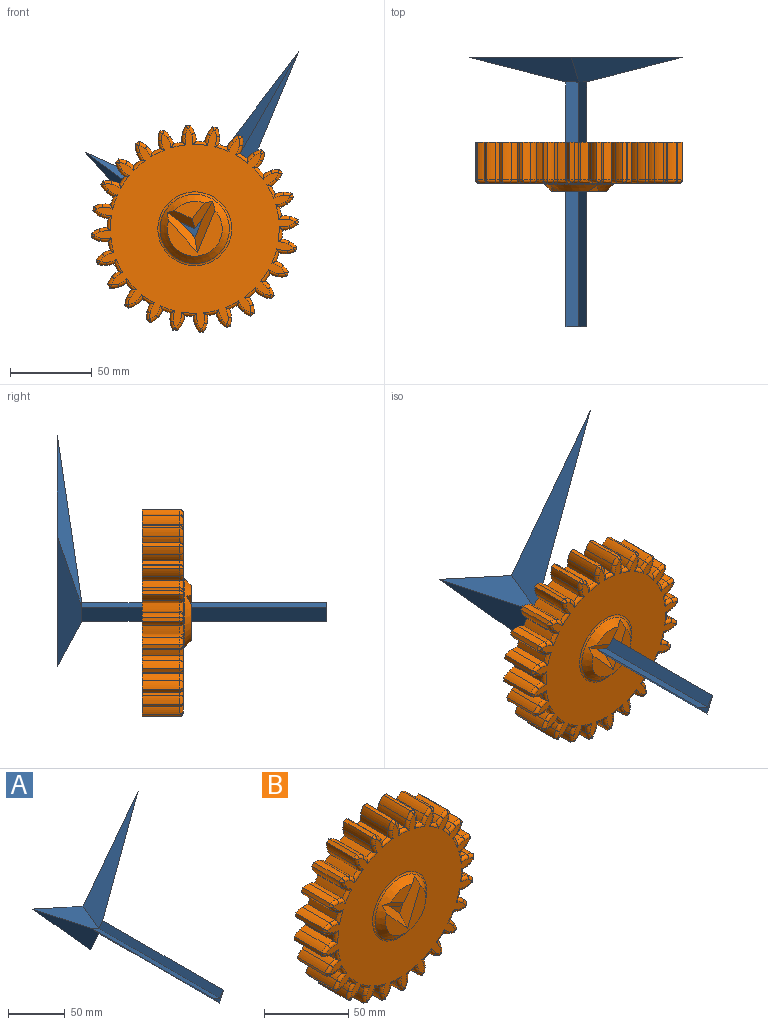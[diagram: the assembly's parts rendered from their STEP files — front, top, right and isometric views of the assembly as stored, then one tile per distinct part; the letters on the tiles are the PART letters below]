
ASSEMBLY  parts=2 mates=1
PART A: 10 faces, bbox 130.9x165x141.5 mm
  f0: plane 150x6.29mm, normal (-0.8,0,0.61), area 1184.6mm2, adj f1,f3,f4,f5
  f1: plane 150x7.89mm, normal (0.41,0,0.91), area 1299.2mm2, adj f0,f2,f4,f8
  f2: plane 150x8.75mm, normal (-0.74,0,-0.67), area 1767mm2, adj f1,f3,f4,f7
  f3: plane 150x11.46mm, normal (0.92,0,-0.38), area 1861.9mm2, adj f0,f2,f4,f6
  f4: plane 12.66x11.46mm, normal (0,-1,0), area 32.7mm2, adj f0,f1,f2,f3
  f5: plane 108.65x68.42mm, normal (-0.56,-0.71,0.43), area 1283.2mm2, adj f0,f6,f8,f9
  f6: plane 141.47x63.72mm, normal (0.65,-0.71,-0.27), area 1757.4mm2, adj f3,f5,f7,f9
  f7: plane 79.84x71.93mm, normal (-0.53,-0.71,-0.47), area 1264.8mm2, adj f2,f6,f8,f9
  f8: plane 67.21x47.02mm, normal (0.29,-0.71,0.64), area 820.2mm2, adj f1,f5,f7,f9
  f9: plane 141.47x130.94mm, normal (0,1,0), area 3657mm2, adj f5,f6,f7,f8
PART B: 302 faces, bbox 127.2x30x127.2 mm
  f0: plane 18.26x10.6mm, normal (0,-1,0), area 107.7mm2, adj f154,f155,f156
  f1: cylinder r=53.72mm len=23mm, axis (0,1,0), area 121.2mm2, adj f29,f31,f96,f289
  f2: cylinder r=53.72mm len=23mm, axis (0,1,0), area 121.2mm2, adj f31,f91,f95,f277
  f3: cylinder r=53.72mm len=23mm, axis (0,1,0), area 121.2mm2, adj f31,f86,f90,f265
  f4: cylinder r=53.72mm len=23mm, axis (0,1,0), area 121.2mm2, adj f31,f81,f85,f253
  f5: cylinder r=53.72mm len=23mm, axis (0,1,0), area 121.2mm2, adj f31,f76,f80,f241
  f6: cylinder r=53.72mm len=23mm, axis (0,1,0), area 121.2mm2, adj f31,f71,f75,f229
  f7: cylinder r=53.72mm len=23mm, axis (0,1,0), area 121.2mm2, adj f31,f66,f70,f217
  f8: cylinder r=53.72mm len=23mm, axis (0,1,0), area 121.2mm2, adj f31,f61,f65,f205
  f9: cylinder r=53.72mm len=23mm, axis (0,1,0), area 121.2mm2, adj f31,f56,f60,f193
  f10: cylinder r=53.72mm len=23mm, axis (0,1,0), area 121.2mm2, adj f31,f51,f55,f181
  f11: cylinder r=53.72mm len=23mm, axis (0,1,0), area 121.2mm2, adj f31,f46,f50,f169
  f12: cylinder r=53.72mm len=23mm, axis (0,1,0), area 121.2mm2, adj f31,f41,f45,f157
  f13: cylinder r=53.72mm len=23mm, axis (0,1,0), area 121.2mm2, adj f31,f40,f147,f168
  f14: cylinder r=53.72mm len=23mm, axis (0,1,0), area 121.2mm2, adj f31,f146,f151,f180
  f15: cylinder r=53.72mm len=23mm, axis (0,1,0), area 121.2mm2, adj f31,f141,f145,f192
  f16: cylinder r=53.72mm len=23mm, axis (0,1,0), area 121.2mm2, adj f31,f136,f140,f204
  f17: cylinder r=53.72mm len=23mm, axis (0,1,0), area 121.2mm2, adj f31,f131,f135,f216
  f18: cylinder r=53.72mm len=23mm, axis (0,1,0), area 121.2mm2, adj f31,f126,f130,f228
  f19: cylinder r=53.72mm len=23mm, axis (0,1,0), area 121.2mm2, adj f31,f121,f125,f240
  f20: cylinder r=53.72mm len=23mm, axis (0,1,0), area 121.2mm2, adj f31,f116,f120,f252
  f21: cylinder r=53.72mm len=23mm, axis (0,1,0), area 121.2mm2, adj f31,f111,f115,f264
  f22: cylinder r=53.72mm len=23mm, axis (0,1,0), area 121.2mm2, adj f31,f106,f110,f276
  f23: cylinder r=53.72mm len=23mm, axis (0,1,0), area 121.2mm2, adj f31,f100,f105,f288
  f24: cylinder r=53.72mm len=23mm, axis (0,1,0), area 121.2mm2, adj f25,f31,f101,f300
  f25: cylinder r=14.37mm len=23mm, axis (0,1,0), area 116.5mm2, adj f24,f26,f31,f299
  f26: cylinder r=14.83mm len=23mm, axis (0,1,0), area 128.5mm2, adj f25,f27,f31,f297
  f27: cylinder r=36.75mm len=23mm, axis (0,1,0), area 59.7mm2, adj f26,f28,f31,f295
  f28: cylinder r=14.83mm len=23mm, axis (0,1,0), area 128.5mm2, adj f27,f29,f31,f293
  f29: cylinder r=14.37mm len=23mm, axis (0,1,0), area 116.5mm2, adj f1,f28,f31,f291
  f30: plane 122.71x122.71mm, normal (0,-1,0), area 7685.4mm2, adj f157,f158,f159,f160,f161,f162,f163,f164
  f31: plane 126.87x126.87mm, normal (0,1,0), area 10687.8mm2, adj f1,f2,f3,f4,f5,f6,f7,f8
  f32: plane 25x6.29mm, normal (0.8,0,-0.61), area 197.4mm2, adj f31,f33,f36,f155
  f33: plane 25x11.46mm, normal (-0.92,0,0.38), area 310.3mm2, adj f31,f32,f34,f152
  f34: plane 25x8.75mm, normal (0.74,0,0.67), area 294.5mm2, adj f31,f33,f36,f153
  f35: plane 33.61x28.22mm, normal (0,-1,0), area 384mm2, adj f152,f153,f154
  f36: plane 25x7.89mm, normal (-0.41,0,-0.91), area 216.5mm2, adj f31,f32,f34,f156
  f37: cylinder r=14.83mm len=23mm, axis (0,1,0), area 128.5mm2, adj f31,f38,f41,f160
  f38: cylinder r=36.75mm len=23mm, axis (0,1,0), area 59.7mm2, adj f31,f37,f39,f162
  f39: cylinder r=14.83mm len=23mm, axis (0,1,0), area 128.5mm2, adj f31,f38,f40,f164
  f40: cylinder r=14.37mm len=23mm, axis (0,1,0), area 116.5mm2, adj f13,f31,f39,f166
  f41: cylinder r=14.37mm len=23mm, axis (0,1,0), area 116.5mm2, adj f12,f31,f37,f158
  f42: cylinder r=14.83mm len=23mm, axis (0,1,0), area 128.5mm2, adj f31,f43,f46,f165
  f43: cylinder r=36.75mm len=23mm, axis (0,1,0), area 59.7mm2, adj f31,f42,f44,f163
  f44: cylinder r=14.83mm len=23mm, axis (0,1,0), area 128.5mm2, adj f31,f43,f45,f161
  f45: cylinder r=14.37mm len=23mm, axis (0,1,0), area 116.5mm2, adj f12,f31,f44,f159
  f46: cylinder r=14.37mm len=23mm, axis (0,1,0), area 116.5mm2, adj f11,f31,f42,f167
  f47: cylinder r=14.83mm len=23mm, axis (0,1,0), area 128.5mm2, adj f31,f48,f51,f177
  f48: cylinder r=36.75mm len=23mm, axis (0,1,0), area 59.7mm2, adj f31,f47,f49,f175
  f49: cylinder r=14.83mm len=23mm, axis (0,1,0), area 128.5mm2, adj f31,f48,f50,f173
  f50: cylinder r=14.37mm len=23mm, axis (0,1,0), area 116.5mm2, adj f11,f31,f49,f171
  f51: cylinder r=14.37mm len=23mm, axis (0,1,0), area 116.5mm2, adj f10,f31,f47,f179
  f52: cylinder r=14.83mm len=23mm, axis (0,1,0), area 128.5mm2, adj f31,f53,f56,f189
  f53: cylinder r=36.75mm len=23mm, axis (0,1,0), area 59.7mm2, adj f31,f52,f54,f187
  f54: cylinder r=14.83mm len=23mm, axis (0,1,0), area 128.5mm2, adj f31,f53,f55,f185
  f55: cylinder r=14.37mm len=23mm, axis (0,1,0), area 116.5mm2, adj f10,f31,f54,f183
  f56: cylinder r=14.37mm len=23mm, axis (0,1,0), area 116.5mm2, adj f9,f31,f52,f191
  f57: cylinder r=14.83mm len=23mm, axis (0,1,0), area 128.5mm2, adj f31,f58,f61,f201
  f58: cylinder r=36.75mm len=23mm, axis (0,1,0), area 59.7mm2, adj f31,f57,f59,f199
  f59: cylinder r=14.83mm len=23mm, axis (0,1,0), area 128.5mm2, adj f31,f58,f60,f197
  f60: cylinder r=14.37mm len=23mm, axis (0,1,0), area 116.5mm2, adj f9,f31,f59,f195
  f61: cylinder r=14.37mm len=23mm, axis (0,1,0), area 116.5mm2, adj f8,f31,f57,f203
  f62: cylinder r=14.83mm len=23mm, axis (0,1,0), area 128.5mm2, adj f31,f63,f66,f213
  f63: cylinder r=36.75mm len=23mm, axis (0,1,0), area 59.7mm2, adj f31,f62,f64,f211
  f64: cylinder r=14.83mm len=23mm, axis (0,1,0), area 128.5mm2, adj f31,f63,f65,f209
  f65: cylinder r=14.37mm len=23mm, axis (0,1,0), area 116.5mm2, adj f8,f31,f64,f207
  f66: cylinder r=14.37mm len=23mm, axis (0,1,0), area 116.5mm2, adj f7,f31,f62,f215
  f67: cylinder r=14.83mm len=23mm, axis (0,1,0), area 128.5mm2, adj f31,f68,f71,f225
  f68: cylinder r=36.75mm len=23mm, axis (0,1,0), area 59.7mm2, adj f31,f67,f69,f223
  f69: cylinder r=14.83mm len=23mm, axis (0,1,0), area 128.5mm2, adj f31,f68,f70,f221
  f70: cylinder r=14.37mm len=23mm, axis (0,1,0), area 116.5mm2, adj f7,f31,f69,f219
  f71: cylinder r=14.37mm len=23mm, axis (0,1,0), area 116.5mm2, adj f6,f31,f67,f227
  f72: cylinder r=14.83mm len=23mm, axis (0,1,0), area 128.5mm2, adj f31,f73,f76,f237
  f73: cylinder r=36.75mm len=23mm, axis (0,1,0), area 59.7mm2, adj f31,f72,f74,f235
  f74: cylinder r=14.83mm len=23mm, axis (0,1,0), area 128.5mm2, adj f31,f73,f75,f233
  f75: cylinder r=14.37mm len=23mm, axis (0,1,0), area 116.5mm2, adj f6,f31,f74,f231
  f76: cylinder r=14.37mm len=23mm, axis (0,1,0), area 116.5mm2, adj f5,f31,f72,f239
  f77: cylinder r=14.83mm len=23mm, axis (0,1,0), area 128.5mm2, adj f31,f78,f81,f249
  f78: cylinder r=36.75mm len=23mm, axis (0,1,0), area 59.7mm2, adj f31,f77,f79,f247
  f79: cylinder r=14.83mm len=23mm, axis (0,1,0), area 128.5mm2, adj f31,f78,f80,f245
  f80: cylinder r=14.37mm len=23mm, axis (0,1,0), area 116.5mm2, adj f5,f31,f79,f243
  f81: cylinder r=14.37mm len=23mm, axis (0,1,0), area 116.5mm2, adj f4,f31,f77,f251
  f82: cylinder r=14.83mm len=23mm, axis (0,1,0), area 128.5mm2, adj f31,f83,f86,f261
  f83: cylinder r=36.75mm len=23mm, axis (0,1,0), area 59.7mm2, adj f31,f82,f84,f259
  f84: cylinder r=14.83mm len=23mm, axis (0,1,0), area 128.5mm2, adj f31,f83,f85,f257
  f85: cylinder r=14.37mm len=23mm, axis (0,1,0), area 116.5mm2, adj f4,f31,f84,f255
  f86: cylinder r=14.37mm len=23mm, axis (0,1,0), area 116.5mm2, adj f3,f31,f82,f263
  f87: cylinder r=14.83mm len=23mm, axis (0,1,0), area 128.5mm2, adj f31,f88,f91,f273
  f88: cylinder r=36.75mm len=23mm, axis (0,1,0), area 59.7mm2, adj f31,f87,f89,f271
  f89: cylinder r=14.83mm len=23mm, axis (0,1,0), area 128.5mm2, adj f31,f88,f90,f269
  f90: cylinder r=14.37mm len=23mm, axis (0,1,0), area 116.5mm2, adj f3,f31,f89,f267
  f91: cylinder r=14.37mm len=23mm, axis (0,1,0), area 116.5mm2, adj f2,f31,f87,f275
  f92: cylinder r=14.83mm len=23mm, axis (0,1,0), area 128.5mm2, adj f31,f93,f96,f285
  f93: cylinder r=36.75mm len=23mm, axis (0,1,0), area 59.7mm2, adj f31,f92,f94,f283
  f94: cylinder r=14.83mm len=23mm, axis (0,1,0), area 128.5mm2, adj f31,f93,f95,f281
  f95: cylinder r=14.37mm len=23mm, axis (0,1,0), area 116.5mm2, adj f2,f31,f94,f279
  f96: cylinder r=14.37mm len=23mm, axis (0,1,0), area 116.5mm2, adj f1,f31,f92,f287
  f97: cylinder r=14.83mm len=23mm, axis (0,1,0), area 128.5mm2, adj f31,f98,f100,f292
  f98: cylinder r=36.75mm len=23mm, axis (0,1,0), area 59.7mm2, adj f31,f97,f99,f294
  f99: cylinder r=14.83mm len=23mm, axis (0,1,0), area 128.5mm2, adj f31,f98,f101,f296
  f100: cylinder r=14.37mm len=23mm, axis (0,1,0), area 116.5mm2, adj f23,f31,f97,f290
  f101: cylinder r=14.37mm len=23mm, axis (0,1,0), area 116.5mm2, adj f24,f31,f99,f298
  f102: cylinder r=14.83mm len=23mm, axis (0,1,0), area 128.5mm2, adj f31,f103,f106,f280
  f103: cylinder r=36.75mm len=23mm, axis (0,1,0), area 59.7mm2, adj f31,f102,f104,f282
  f104: cylinder r=14.83mm len=23mm, axis (0,1,0), area 128.5mm2, adj f31,f103,f105,f284
  f105: cylinder r=14.37mm len=23mm, axis (0,1,0), area 116.5mm2, adj f23,f31,f104,f286
  f106: cylinder r=14.37mm len=23mm, axis (0,1,0), area 116.5mm2, adj f22,f31,f102,f278
  f107: cylinder r=14.83mm len=23mm, axis (0,1,0), area 128.5mm2, adj f31,f108,f111,f268
  f108: cylinder r=36.75mm len=23mm, axis (0,1,0), area 59.7mm2, adj f31,f107,f109,f270
  f109: cylinder r=14.83mm len=23mm, axis (0,1,0), area 128.5mm2, adj f31,f108,f110,f272
  f110: cylinder r=14.37mm len=23mm, axis (0,1,0), area 116.5mm2, adj f22,f31,f109,f274
  f111: cylinder r=14.37mm len=23mm, axis (0,1,0), area 116.5mm2, adj f21,f31,f107,f266
  f112: cylinder r=14.83mm len=23mm, axis (0,1,0), area 128.5mm2, adj f31,f113,f116,f256
  f113: cylinder r=36.75mm len=23mm, axis (0,1,0), area 59.7mm2, adj f31,f112,f114,f258
  f114: cylinder r=14.83mm len=23mm, axis (0,1,0), area 128.5mm2, adj f31,f113,f115,f260
  f115: cylinder r=14.37mm len=23mm, axis (0,1,0), area 116.5mm2, adj f21,f31,f114,f262
  f116: cylinder r=14.37mm len=23mm, axis (0,1,0), area 116.5mm2, adj f20,f31,f112,f254
  f117: cylinder r=14.83mm len=23mm, axis (0,1,0), area 128.5mm2, adj f31,f118,f121,f244
  f118: cylinder r=36.75mm len=23mm, axis (0,1,0), area 59.7mm2, adj f31,f117,f119,f246
  f119: cylinder r=14.83mm len=23mm, axis (0,1,0), area 128.5mm2, adj f31,f118,f120,f248
  f120: cylinder r=14.37mm len=23mm, axis (0,1,0), area 116.5mm2, adj f20,f31,f119,f250
  f121: cylinder r=14.37mm len=23mm, axis (0,1,0), area 116.5mm2, adj f19,f31,f117,f242
  f122: cylinder r=14.83mm len=23mm, axis (0,1,0), area 128.5mm2, adj f31,f123,f126,f232
  f123: cylinder r=36.75mm len=23mm, axis (0,1,0), area 59.7mm2, adj f31,f122,f124,f234
  f124: cylinder r=14.83mm len=23mm, axis (0,1,0), area 128.5mm2, adj f31,f123,f125,f236
  f125: cylinder r=14.37mm len=23mm, axis (0,1,0), area 116.5mm2, adj f19,f31,f124,f238
  f126: cylinder r=14.37mm len=23mm, axis (0,1,0), area 116.5mm2, adj f18,f31,f122,f230
  f127: cylinder r=14.83mm len=23mm, axis (0,1,0), area 128.5mm2, adj f31,f128,f131,f220
  f128: cylinder r=36.75mm len=23mm, axis (0,1,0), area 59.7mm2, adj f31,f127,f129,f222
  f129: cylinder r=14.83mm len=23mm, axis (0,1,0), area 128.5mm2, adj f31,f128,f130,f224
  f130: cylinder r=14.37mm len=23mm, axis (0,1,0), area 116.5mm2, adj f18,f31,f129,f226
  f131: cylinder r=14.37mm len=23mm, axis (0,1,0), area 116.5mm2, adj f17,f31,f127,f218
  f132: cylinder r=14.83mm len=23mm, axis (0,1,0), area 128.5mm2, adj f31,f133,f136,f208
  f133: cylinder r=36.75mm len=23mm, axis (0,1,0), area 59.7mm2, adj f31,f132,f134,f210
  f134: cylinder r=14.83mm len=23mm, axis (0,1,0), area 128.5mm2, adj f31,f133,f135,f212
  f135: cylinder r=14.37mm len=23mm, axis (0,1,0), area 116.5mm2, adj f17,f31,f134,f214
  f136: cylinder r=14.37mm len=23mm, axis (0,1,0), area 116.5mm2, adj f16,f31,f132,f206
  f137: cylinder r=14.83mm len=23mm, axis (0,1,0), area 128.5mm2, adj f31,f138,f141,f196
  f138: cylinder r=36.75mm len=23mm, axis (0,1,0), area 59.7mm2, adj f31,f137,f139,f198
  f139: cylinder r=14.83mm len=23mm, axis (0,1,0), area 128.5mm2, adj f31,f138,f140,f200
  f140: cylinder r=14.37mm len=23mm, axis (0,1,0), area 116.5mm2, adj f16,f31,f139,f202
  f141: cylinder r=14.37mm len=23mm, axis (0,1,0), area 116.5mm2, adj f15,f31,f137,f194
  f142: cylinder r=14.83mm len=23mm, axis (0,1,0), area 128.5mm2, adj f31,f143,f146,f184
  f143: cylinder r=36.75mm len=23mm, axis (0,1,0), area 59.7mm2, adj f31,f142,f144,f186
  f144: cylinder r=14.83mm len=23mm, axis (0,1,0), area 128.5mm2, adj f31,f143,f145,f188
  f145: cylinder r=14.37mm len=23mm, axis (0,1,0), area 116.5mm2, adj f15,f31,f144,f190
  f146: cylinder r=14.37mm len=23mm, axis (0,1,0), area 116.5mm2, adj f14,f31,f142,f182
  f147: cylinder r=14.37mm len=23mm, axis (0,1,0), area 116.5mm2, adj f13,f31,f148,f170
  f148: cylinder r=14.83mm len=23mm, axis (0,1,0), area 128.5mm2, adj f31,f147,f149,f172
  f149: cylinder r=36.75mm len=23mm, axis (0,1,0), area 59.7mm2, adj f31,f148,f150,f174
  f150: cylinder r=14.83mm len=23mm, axis (0,1,0), area 128.5mm2, adj f31,f149,f151,f176
  f151: cylinder r=14.37mm len=23mm, axis (0,1,0), area 116.5mm2, adj f14,f31,f150,f178
  f152: plane 31.4x12.33mm, normal (-0.65,-0.71,0.27), area 178.1mm2, adj f33,f35,f153,f154,f155
  f153: plane 24.47x18.34mm, normal (0.53,-0.71,0.47), area 162.5mm2, adj f34,f35,f152,f154,f156
  f154: cone r=16.8mm half-angle=45deg, axis (0,1,0), area 713mm2, adj f0,f35,f152,f153,f155,f156,f301
  f155: plane 17.01x12.52mm, normal (0.56,-0.71,-0.43), area 105.3mm2, adj f0,f32,f152,f154,f156
  f156: plane 16.76x11.19mm, normal (-0.29,-0.71,-0.64), area 99.8mm2, adj f0,f36,f153,f154,f155
  f157: torus R=51.72mm, axis (0,-1,0), area 21mm2, adj f12,f30,f158,f159
  f158: torus R=12.37mm, axis (0,-1,0), area 17.4mm2, adj f30,f41,f157,f160
  f159: torus R=12.37mm, axis (0,-1,0), area 17.4mm2, adj f30,f45,f157,f161
  f160: torus R=12.83mm, axis (0,-1,0), area 15.6mm2, adj f30,f37,f158,f162
  f161: torus R=12.83mm, axis (0,-1,0), area 15.6mm2, adj f30,f44,f159,f163
  f162: torus R=38.75mm, axis (0,-1,0), area 5.9mm2, adj f30,f38,f160,f164
  f163: torus R=38.75mm, axis (0,-1,0), area 5.9mm2, adj f30,f43,f161,f165
  f164: torus R=12.83mm, axis (0,-1,0), area 15.6mm2, adj f30,f39,f162,f166
  f165: torus R=12.83mm, axis (0,-1,0), area 15.6mm2, adj f30,f42,f163,f167
  f166: torus R=12.37mm, axis (0,-1,0), area 17.4mm2, adj f30,f40,f164,f168
  f167: torus R=12.37mm, axis (0,-1,0), area 17.4mm2, adj f30,f46,f165,f169
  f168: torus R=51.72mm, axis (0,-1,0), area 21mm2, adj f13,f30,f166,f170
  f169: torus R=51.72mm, axis (0,-1,0), area 21mm2, adj f11,f30,f167,f171
  f170: torus R=12.37mm, axis (0,-1,0), area 17.4mm2, adj f30,f147,f168,f172
  f171: torus R=12.37mm, axis (0,-1,0), area 17.4mm2, adj f30,f50,f169,f173
  f172: torus R=12.83mm, axis (0,-1,0), area 15.6mm2, adj f30,f148,f170,f174
  f173: torus R=12.83mm, axis (0,-1,0), area 15.6mm2, adj f30,f49,f171,f175
  f174: torus R=38.75mm, axis (0,-1,0), area 5.9mm2, adj f30,f149,f172,f176
  f175: torus R=38.75mm, axis (0,-1,0), area 5.9mm2, adj f30,f48,f173,f177
  f176: torus R=12.83mm, axis (0,-1,0), area 15.6mm2, adj f30,f150,f174,f178
  f177: torus R=12.83mm, axis (0,-1,0), area 15.6mm2, adj f30,f47,f175,f179
  f178: torus R=12.37mm, axis (0,-1,0), area 17.4mm2, adj f30,f151,f176,f180
  f179: torus R=12.37mm, axis (0,-1,0), area 17.4mm2, adj f30,f51,f177,f181
  f180: torus R=51.72mm, axis (0,-1,0), area 21mm2, adj f14,f30,f178,f182
  f181: torus R=51.72mm, axis (0,-1,0), area 21mm2, adj f10,f30,f179,f183
  f182: torus R=12.37mm, axis (0,-1,0), area 17.4mm2, adj f30,f146,f180,f184
  f183: torus R=12.37mm, axis (0,-1,0), area 17.4mm2, adj f30,f55,f181,f185
  f184: torus R=12.83mm, axis (0,-1,0), area 15.6mm2, adj f30,f142,f182,f186
  f185: torus R=12.83mm, axis (0,-1,0), area 15.6mm2, adj f30,f54,f183,f187
  f186: torus R=38.75mm, axis (0,-1,0), area 5.9mm2, adj f30,f143,f184,f188
  f187: torus R=38.75mm, axis (0,-1,0), area 5.9mm2, adj f30,f53,f185,f189
  f188: torus R=12.83mm, axis (0,-1,0), area 15.6mm2, adj f30,f144,f186,f190
  f189: torus R=12.83mm, axis (0,-1,0), area 15.6mm2, adj f30,f52,f187,f191
  f190: torus R=12.37mm, axis (0,-1,0), area 17.4mm2, adj f30,f145,f188,f192
  f191: torus R=12.37mm, axis (0,-1,0), area 17.4mm2, adj f30,f56,f189,f193
  f192: torus R=51.72mm, axis (0,-1,0), area 21mm2, adj f15,f30,f190,f194
  f193: torus R=51.72mm, axis (0,-1,0), area 21mm2, adj f9,f30,f191,f195
  f194: torus R=12.37mm, axis (0,-1,0), area 17.4mm2, adj f30,f141,f192,f196
  f195: torus R=12.37mm, axis (0,-1,0), area 17.4mm2, adj f30,f60,f193,f197
  f196: torus R=12.83mm, axis (0,-1,0), area 15.6mm2, adj f30,f137,f194,f198
  f197: torus R=12.83mm, axis (0,-1,0), area 15.6mm2, adj f30,f59,f195,f199
  f198: torus R=38.75mm, axis (0,-1,0), area 5.9mm2, adj f30,f138,f196,f200
  f199: torus R=38.75mm, axis (0,-1,0), area 5.9mm2, adj f30,f58,f197,f201
  f200: torus R=12.83mm, axis (0,-1,0), area 15.6mm2, adj f30,f139,f198,f202
  f201: torus R=12.83mm, axis (0,-1,0), area 15.6mm2, adj f30,f57,f199,f203
  f202: torus R=12.37mm, axis (0,-1,0), area 17.4mm2, adj f30,f140,f200,f204
  f203: torus R=12.37mm, axis (0,-1,0), area 17.4mm2, adj f30,f61,f201,f205
  f204: torus R=51.72mm, axis (0,-1,0), area 21mm2, adj f16,f30,f202,f206
  f205: torus R=51.72mm, axis (0,-1,0), area 21mm2, adj f8,f30,f203,f207
  f206: torus R=12.37mm, axis (0,-1,0), area 17.4mm2, adj f30,f136,f204,f208
  f207: torus R=12.37mm, axis (0,-1,0), area 17.4mm2, adj f30,f65,f205,f209
  f208: torus R=12.83mm, axis (0,-1,0), area 15.6mm2, adj f30,f132,f206,f210
  f209: torus R=12.83mm, axis (0,-1,0), area 15.6mm2, adj f30,f64,f207,f211
  f210: torus R=38.75mm, axis (0,-1,0), area 5.9mm2, adj f30,f133,f208,f212
  f211: torus R=38.75mm, axis (0,-1,0), area 5.9mm2, adj f30,f63,f209,f213
  f212: torus R=12.83mm, axis (0,-1,0), area 15.6mm2, adj f30,f134,f210,f214
  f213: torus R=12.83mm, axis (0,-1,0), area 15.6mm2, adj f30,f62,f211,f215
  f214: torus R=12.37mm, axis (0,-1,0), area 17.4mm2, adj f30,f135,f212,f216
  f215: torus R=12.37mm, axis (0,-1,0), area 17.4mm2, adj f30,f66,f213,f217
  f216: torus R=51.72mm, axis (0,-1,0), area 21mm2, adj f17,f30,f214,f218
  f217: torus R=51.72mm, axis (0,-1,0), area 21mm2, adj f7,f30,f215,f219
  f218: torus R=12.37mm, axis (0,-1,0), area 17.4mm2, adj f30,f131,f216,f220
  f219: torus R=12.37mm, axis (0,-1,0), area 17.4mm2, adj f30,f70,f217,f221
  f220: torus R=12.83mm, axis (0,-1,0), area 15.6mm2, adj f30,f127,f218,f222
  f221: torus R=12.83mm, axis (0,-1,0), area 15.6mm2, adj f30,f69,f219,f223
  f222: torus R=38.75mm, axis (0,-1,0), area 5.9mm2, adj f30,f128,f220,f224
  f223: torus R=38.75mm, axis (0,-1,0), area 5.9mm2, adj f30,f68,f221,f225
  f224: torus R=12.83mm, axis (0,-1,0), area 15.6mm2, adj f30,f129,f222,f226
  f225: torus R=12.83mm, axis (0,-1,0), area 15.6mm2, adj f30,f67,f223,f227
  f226: torus R=12.37mm, axis (0,-1,0), area 17.4mm2, adj f30,f130,f224,f228
  f227: torus R=12.37mm, axis (0,-1,0), area 17.4mm2, adj f30,f71,f225,f229
  f228: torus R=51.72mm, axis (0,-1,0), area 21mm2, adj f18,f30,f226,f230
  f229: torus R=51.72mm, axis (0,-1,0), area 21mm2, adj f6,f30,f227,f231
  f230: torus R=12.37mm, axis (0,-1,0), area 17.4mm2, adj f30,f126,f228,f232
  f231: torus R=12.37mm, axis (0,-1,0), area 17.4mm2, adj f30,f75,f229,f233
  f232: torus R=12.83mm, axis (0,-1,0), area 15.6mm2, adj f30,f122,f230,f234
  f233: torus R=12.83mm, axis (0,-1,0), area 15.6mm2, adj f30,f74,f231,f235
  f234: torus R=38.75mm, axis (0,-1,0), area 5.9mm2, adj f30,f123,f232,f236
  f235: torus R=38.75mm, axis (0,-1,0), area 5.9mm2, adj f30,f73,f233,f237
  f236: torus R=12.83mm, axis (0,-1,0), area 15.6mm2, adj f30,f124,f234,f238
  f237: torus R=12.83mm, axis (0,-1,0), area 15.6mm2, adj f30,f72,f235,f239
  f238: torus R=12.37mm, axis (0,-1,0), area 17.4mm2, adj f30,f125,f236,f240
  f239: torus R=12.37mm, axis (0,-1,0), area 17.4mm2, adj f30,f76,f237,f241
  f240: torus R=51.72mm, axis (0,-1,0), area 21mm2, adj f19,f30,f238,f242
  f241: torus R=51.72mm, axis (0,-1,0), area 21mm2, adj f5,f30,f239,f243
  f242: torus R=12.37mm, axis (0,-1,0), area 17.4mm2, adj f30,f121,f240,f244
  f243: torus R=12.37mm, axis (0,-1,0), area 17.4mm2, adj f30,f80,f241,f245
  f244: torus R=12.83mm, axis (0,-1,0), area 15.6mm2, adj f30,f117,f242,f246
  f245: torus R=12.83mm, axis (0,-1,0), area 15.6mm2, adj f30,f79,f243,f247
  f246: torus R=38.75mm, axis (0,-1,0), area 5.9mm2, adj f30,f118,f244,f248
  f247: torus R=38.75mm, axis (0,-1,0), area 5.9mm2, adj f30,f78,f245,f249
  f248: torus R=12.83mm, axis (0,-1,0), area 15.6mm2, adj f30,f119,f246,f250
  f249: torus R=12.83mm, axis (0,-1,0), area 15.6mm2, adj f30,f77,f247,f251
  f250: torus R=12.37mm, axis (0,-1,0), area 17.4mm2, adj f30,f120,f248,f252
  f251: torus R=12.37mm, axis (0,-1,0), area 17.4mm2, adj f30,f81,f249,f253
  f252: torus R=51.72mm, axis (0,-1,0), area 21mm2, adj f20,f30,f250,f254
  f253: torus R=51.72mm, axis (0,-1,0), area 21mm2, adj f4,f30,f251,f255
  f254: torus R=12.37mm, axis (0,-1,0), area 17.4mm2, adj f30,f116,f252,f256
  f255: torus R=12.37mm, axis (0,-1,0), area 17.4mm2, adj f30,f85,f253,f257
  f256: torus R=12.83mm, axis (0,-1,0), area 15.6mm2, adj f30,f112,f254,f258
  f257: torus R=12.83mm, axis (0,-1,0), area 15.6mm2, adj f30,f84,f255,f259
  f258: torus R=38.75mm, axis (0,-1,0), area 5.9mm2, adj f30,f113,f256,f260
  f259: torus R=38.75mm, axis (0,-1,0), area 5.9mm2, adj f30,f83,f257,f261
  f260: torus R=12.83mm, axis (0,-1,0), area 15.6mm2, adj f30,f114,f258,f262
  f261: torus R=12.83mm, axis (0,-1,0), area 15.6mm2, adj f30,f82,f259,f263
  f262: torus R=12.37mm, axis (0,-1,0), area 17.4mm2, adj f30,f115,f260,f264
  f263: torus R=12.37mm, axis (0,-1,0), area 17.4mm2, adj f30,f86,f261,f265
  f264: torus R=51.72mm, axis (0,-1,0), area 21mm2, adj f21,f30,f262,f266
  f265: torus R=51.72mm, axis (0,-1,0), area 21mm2, adj f3,f30,f263,f267
  f266: torus R=12.37mm, axis (0,-1,0), area 17.4mm2, adj f30,f111,f264,f268
  f267: torus R=12.37mm, axis (0,-1,0), area 17.4mm2, adj f30,f90,f265,f269
  f268: torus R=12.83mm, axis (0,-1,0), area 15.6mm2, adj f30,f107,f266,f270
  f269: torus R=12.83mm, axis (0,-1,0), area 15.6mm2, adj f30,f89,f267,f271
  f270: torus R=38.75mm, axis (0,-1,0), area 5.9mm2, adj f30,f108,f268,f272
  f271: torus R=38.75mm, axis (0,-1,0), area 5.9mm2, adj f30,f88,f269,f273
  f272: torus R=12.83mm, axis (0,-1,0), area 15.6mm2, adj f30,f109,f270,f274
  f273: torus R=12.83mm, axis (0,-1,0), area 15.6mm2, adj f30,f87,f271,f275
  f274: torus R=12.37mm, axis (0,-1,0), area 17.4mm2, adj f30,f110,f272,f276
  f275: torus R=12.37mm, axis (0,-1,0), area 17.4mm2, adj f30,f91,f273,f277
  f276: torus R=51.72mm, axis (0,-1,0), area 21mm2, adj f22,f30,f274,f278
  f277: torus R=51.72mm, axis (0,-1,0), area 21mm2, adj f2,f30,f275,f279
  f278: torus R=12.37mm, axis (0,-1,0), area 17.4mm2, adj f30,f106,f276,f280
  f279: torus R=12.37mm, axis (0,-1,0), area 17.4mm2, adj f30,f95,f277,f281
  f280: torus R=12.83mm, axis (0,-1,0), area 15.6mm2, adj f30,f102,f278,f282
  f281: torus R=12.83mm, axis (0,-1,0), area 15.6mm2, adj f30,f94,f279,f283
  f282: torus R=38.75mm, axis (0,-1,0), area 5.9mm2, adj f30,f103,f280,f284
  f283: torus R=38.75mm, axis (0,-1,0), area 5.9mm2, adj f30,f93,f281,f285
  f284: torus R=12.83mm, axis (0,-1,0), area 15.6mm2, adj f30,f104,f282,f286
  f285: torus R=12.83mm, axis (0,-1,0), area 15.6mm2, adj f30,f92,f283,f287
  f286: torus R=12.37mm, axis (0,-1,0), area 17.4mm2, adj f30,f105,f284,f288
  f287: torus R=12.37mm, axis (0,-1,0), area 17.4mm2, adj f30,f96,f285,f289
  f288: torus R=51.72mm, axis (0,-1,0), area 21mm2, adj f23,f30,f286,f290
  f289: torus R=51.72mm, axis (0,-1,0), area 21mm2, adj f1,f30,f287,f291
  f290: torus R=12.37mm, axis (0,-1,0), area 17.4mm2, adj f30,f100,f288,f292
  f291: torus R=12.37mm, axis (0,-1,0), area 17.4mm2, adj f29,f30,f289,f293
  f292: torus R=12.83mm, axis (0,-1,0), area 15.6mm2, adj f30,f97,f290,f294
  f293: torus R=12.83mm, axis (0,-1,0), area 15.6mm2, adj f28,f30,f291,f295
  f294: torus R=38.75mm, axis (0,-1,0), area 5.9mm2, adj f30,f98,f292,f296
  f295: torus R=38.75mm, axis (0,-1,0), area 5.9mm2, adj f27,f30,f293,f297
  f296: torus R=12.83mm, axis (0,-1,0), area 15.6mm2, adj f30,f99,f294,f298
  f297: torus R=12.83mm, axis (0,-1,0), area 15.6mm2, adj f26,f30,f295,f299
  f298: torus R=12.37mm, axis (0,-1,0), area 17.4mm2, adj f30,f101,f296,f300
  f299: torus R=12.37mm, axis (0,-1,0), area 17.4mm2, adj f25,f30,f297,f300
  f300: torus R=51.72mm, axis (0,-1,0), area 21mm2, adj f24,f30,f298,f299
  f301: torus R=22.63mm, axis (0,-1,0), area 216mm2, adj f30,f154
PLACE A rot(axis=(-0.95,-0.16,0.25),0deg) t=(27.09,90.35,5.61)mm
PLACE B t=(27.83,53.31,4.5)mm fixed
MATE slider A.f4 <-> B.f0  axis (0,-1,0) through (26.83,-59.65,4.25)mm
